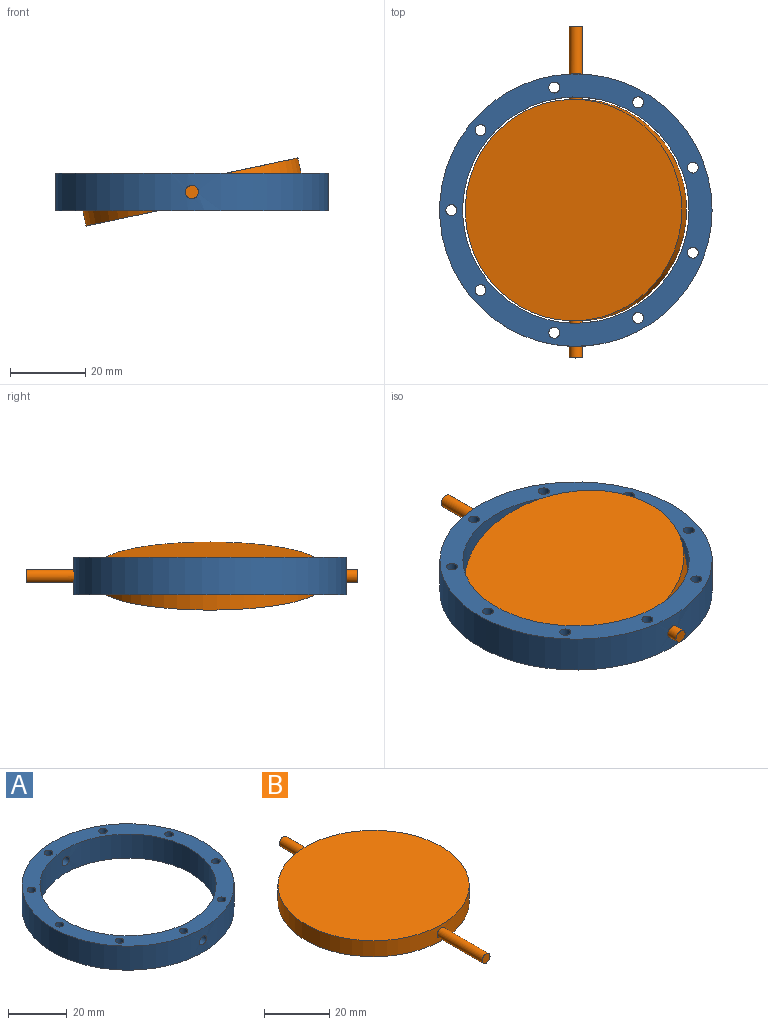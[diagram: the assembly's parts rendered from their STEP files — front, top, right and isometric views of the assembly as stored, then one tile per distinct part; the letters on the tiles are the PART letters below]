
ASSEMBLY  parts=2 mates=1
PART A: 15 faces, bbox 72.2x72.2x10 mm
  f0: cylinder r=30mm len=60mm, axis (0,0,-1), area 1866mm2, adj f11,f12,f13,f14
  f1: cylinder r=36.11mm len=72.22mm, axis (0,0,-1), area 2249.9mm2, adj f11,f12,f13,f14
  f2: cylinder r=1.46mm len=10mm, axis (0,0,-1), area 91.4mm2, adj f11,f12
  f3: cylinder r=1.46mm len=10mm, axis (0,0,-1), area 91.4mm2, adj f11,f12
  f4: cylinder r=1.46mm len=10mm, axis (0,0,-1), area 91.4mm2, adj f11,f12
  f5: cylinder r=1.46mm len=10mm, axis (0,0,-1), area 91.4mm2, adj f11,f12
  f6: cylinder r=1.46mm len=10mm, axis (0,0,-1), area 91.4mm2, adj f11,f12
  f7: cylinder r=1.46mm len=10mm, axis (0,0,-1), area 91.4mm2, adj f11,f12
  f8: cylinder r=1.46mm len=10mm, axis (0,0,-1), area 91.4mm2, adj f11,f12
  f9: cylinder r=1.46mm len=10mm, axis (0,0,-1), area 91.4mm2, adj f11,f12
  f10: cylinder r=1.46mm len=10mm, axis (0,0,-1), area 91.4mm2, adj f11,f12
  f11: plane 72.22x72.22mm, normal (0,0,1), area 1209.1mm2, adj f0,f1,f2,f3,f4,f5,f6,f7
  f12: plane 72.22x72.22mm, normal (0,0,-1), area 1209.1mm2, adj f0,f1,f2,f3,f4,f5,f6,f7
  f13: cylinder r=1.74mm len=6.16mm, axis (0,1,0), area 66.7mm2, adj f0,f1
  f14: cylinder r=1.74mm len=6.16mm, axis (0,1,0), area 66.7mm2, adj f0,f1
PART B: 7 faces, bbox 58.7x88x6 mm
  f0: cylinder r=29.36mm len=58.72mm, axis (0,0,-1), area 1087.9mm2, adj f1,f2,f4,f5
  f1: plane 58.72x58.72mm, normal (0,0,1), area 2708mm2, adj f0
  f2: plane 58.72x58.72mm, normal (0,0,-1), area 2708mm2, adj f0
  f3: plane 3.47x3.47mm, normal (0,1,0), area 9.5mm2, adj f4
  f4: cylinder r=1.74mm len=9.89mm, axis (0,1,0), area 107.6mm2, adj f0,f3
  f5: cylinder r=1.74mm len=19.49mm, axis (0,1,0), area 212.3mm2, adj f0,f6
  f6: plane 3.47x3.47mm, normal (0,-1,0), area 9.5mm2, adj f5
PLACE A at identity fixed
PLACE B rot(axis=(0.99,0,0.1),180deg) t=(-1.04,0.01,9.89)mm
MATE revolute B.f4 <-> A.f13  axis (0,-1,0) through (0,-34.21,5)mm
